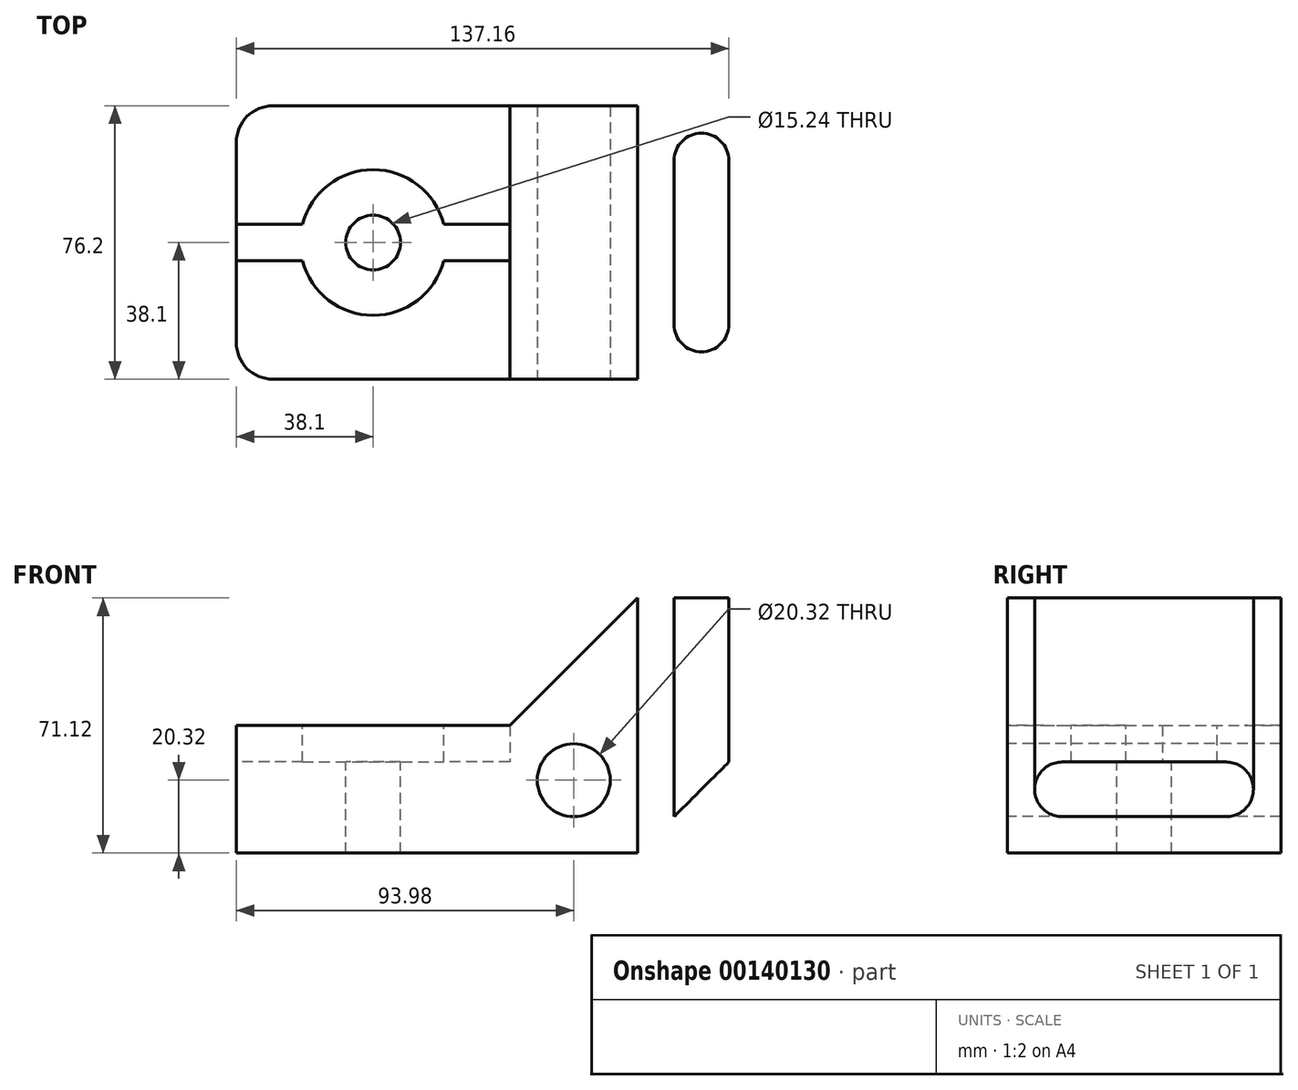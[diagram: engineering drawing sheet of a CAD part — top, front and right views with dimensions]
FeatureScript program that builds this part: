
annotation { "Feature Type Name" : "Feature", "Feature Type Description" : "" }
export const myFeature = defineFeature(function(context is Context, id is Id, definition is map)
    precondition{}
    {
        {
            var Q0;
            Q0=qCreatedBy(makeId("Top.planeOp"),FACE);
            var sketch = newSketch(context, id + "F0", { "sketchPlane" : qUnion([Q0])});
            skLineSegment(sketch, "E0.bottom", {"start": v(0, 0) * mm, "end": v(76.2, 0) * mm});
            skLineSegment(sketch, "E0.top", {"start": v(0, 76.2) * mm, "end": v(76.2, 76.2) * mm});
            skLineSegment(sketch, "E0.left", {"start": v(0, 0) * mm, "end": v(0, 76.2) * mm});
            skLineSegment(sketch, "E0.right", {"start": v(76.2, 0) * mm, "end": v(76.2, 76.2) * mm});
            skLineSegment(sketch, "E1.bottom", {"start": v(76.2, 76.2) * mm, "end": v(147.32, 76.2) * mm});
            skLineSegment(sketch, "E1.top", {"start": v(76.2, 0) * mm, "end": v(147.32, 0) * mm});
            skLineSegment(sketch, "E1.left", {"start": v(76.2, 76.2) * mm, "end": v(76.2, 0) * mm});
            skLineSegment(sketch, "E1.right", {"start": v(147.32, 76.2) * mm, "end": v(147.32, 0) * mm});
            skSolve(sketch);
        }
        {
            var Q0;
            Q0=makeQuery(id+"F0.imprint","IMPRINT",FACE,{"disambiguationData":[TD([[makeQuery(id+"F0.imprint","IMPRINT",EDGE,{"derivedFrom":sQuery(id+"F0.wireOp",EDGE,"E0.bottom")}),1.0]])]});
            extrude(context, id + "F1", {"entities" : qUnion([Q0]), "depth" : 35.56 * mm});
        }
        {
            var Q0;
            Q0=makeQuery(id+"F0.imprint","IMPRINT",FACE,{"disambiguationData":[TD([[makeQuery(id+"F0.imprint","IMPRINT",EDGE,{"derivedFrom":sQuery(id+"F0.wireOp",EDGE,"E1.bottom")}),-1.0]])]});
            extrude(context, id + "F2", {"entities" : qUnion([Q0]), "operationType" : NewBodyOperationType.ADD, "depth" : 71.12 * mm});
        }
        {
            var Q0;
            Q0=makeQuery(id+"F2.boolean.opBoolean","MERGE",FACE,{"derivedFrom":[makeQuery(id+"F1.opExtrude","SWEPT_FACE",FACE,{"disambiguationData":[OSD([sQuery(id+"F0.wireOp",EDGE,"E0.bottom")])]}),makeQuery(id+"F2.opExtrude","SWEPT_FACE",FACE,{"disambiguationData":[OSD([sQuery(id+"F0.wireOp",EDGE,"E1.top")])]})]});
            var sketch = newSketch(context, id + "F3", { "sketchPlane" : qUnion([Q0])});
            skLineSegment(sketch, "E2", {"start": v(147.32, 0) * mm, "end": v(111.76, 0) * mm});
            skLineSegment(sketch, "E3", {"start": v(111.76, 0) * mm, "end": v(147.32, 35.56) * mm});
            skLineSegment(sketch, "E4", {"start": v(147.32, 35.56) * mm, "end": v(147.32, 0) * mm});
            skLineSegment(sketch, "E5", {"start": v(76.2, 35.56) * mm, "end": v(111.76, 71.12) * mm});
            skLineSegment(sketch, "E6", {"start": v(111.76, 71.12) * mm, "end": v(76.2, 71.12) * mm});
            skLineSegment(sketch, "E7", {"start": v(76.2, 71.12) * mm, "end": v(76.2, 35.56) * mm});
            skSolve(sketch);
        }
        {
            var Q0;
            Q0=makeQuery(id+"F3.imprint","IMPRINT",FACE,{"disambiguationData":[TD([[makeQuery(id+"F3.imprint","IMPRINT",EDGE,{"derivedFrom":sQuery(id+"F3.wireOp",EDGE,"E5")}),1.0]])]});
            var Q1;
            Q1=makeQuery(id+"F3.imprint","IMPRINT",FACE,{"disambiguationData":[TD([[makeQuery(id+"F3.imprint","IMPRINT",EDGE,{"derivedFrom":sQuery(id+"F3.wireOp",EDGE,"E2")}),1.0]])]});
            extrude(context, id + "F4", {"entities" : qUnion([Q0, Q1]), "operationType" : NewBodyOperationType.REMOVE, "endBound" : BoundingType.THROUGH_ALL, "oppositeDirection" : true, "depth" : 25.4 * mm});
        }
        {
            var Q0;
            Q0=makeQuery(id+"F2.boolean.opBoolean","MERGE",FACE,{"derivedFrom":[makeQuery(id+"F1.opExtrude","SWEPT_FACE",FACE,{"disambiguationData":[OSD([sQuery(id+"F0.wireOp",EDGE,"E0.bottom")])]}),makeQuery(id+"F2.opExtrude","SWEPT_FACE",FACE,{"disambiguationData":[OSD([sQuery(id+"F0.wireOp",EDGE,"E1.top")])]})]});
            var sketch = newSketch(context, id + "F5", { "sketchPlane" : qUnion([Q0])});
            skCircle(sketch, "E8", {"center": v(93.98, 20.32) * mm, "radius": 10.16 * mm});
            skSolve(sketch);
        }
        {
            var Q0;
            Q0=makeQuery(id+"F5.imprint","IMPRINT",FACE,{"disambiguationData":[TD([[makeQuery(id+"F5.imprint","IMPRINT",EDGE,{"derivedFrom":sQuery(id+"F5.wireOp",EDGE,"E8")}),1.0]])]});
            extrude(context, id + "F6", {"entities" : qUnion([Q0]), "operationType" : NewBodyOperationType.REMOVE, "endBound" : BoundingType.THROUGH_ALL, "oppositeDirection" : true, "depth" : 25.4 * mm});
        }
        {
            var Q0;
            Q0=makeQuery(id+"F2.opExtrude","CAP_FACE",FACE,{"disambiguationData":[OSD([sQuery(id+"F0.wireOp",EDGE,"E1.bottom"),sQuery(id+"F0.wireOp",EDGE,"E1.top"),sQuery(id+"F0.wireOp",EDGE,"E1.left"),sQuery(id+"F0.wireOp",EDGE,"E1.right")])],"isStart":false});
            var sketch = newSketch(context, id + "F7", { "sketchPlane" : qUnion([Q0])});
            skLineSegment(sketch, "E9", {"start": v(147.32, 76.2) * mm, "end": v(129.54, 76.2) * mm, "construction": true});
            skLineSegment(sketch, "E10", {"start": v(129.54, 60.96) * mm, "end": v(129.54, 15.24) * mm, "construction": true});
            skLineSegment(sketch, "E11", {"start": v(129.54, 0) * mm, "end": v(147.32, 0) * mm, "construction": true});
            skPoint(sketch, "E12", {"position": v(129.54, 60.96) * mm});
            skPoint(sketch, "E13", {"position": v(129.54, 15.24) * mm});
            skArc(sketch, "E14.0.startCap", {"start": v(121.92, 60.96) * mm, "mid": v(129.54, 68.58) * mm, "end": v(137.16, 60.96) * mm});
            skArc(sketch, "E14.0.endCap", {"start": v(137.16, 15.24) * mm, "mid": v(129.54, 7.62) * mm, "end": v(121.92, 15.24) * mm});
            skLineSegment(sketch, "E14.0.left", {"start": v(137.16, 60.96) * mm, "end": v(137.16, 15.24) * mm});
            skLineSegment(sketch, "E14.0.right", {"start": v(121.92, 60.96) * mm, "end": v(121.92, 15.24) * mm});
            skSolve(sketch);
        }
        {
            var Q0;
            Q0=makeQuery(id+"F7.imprint","IMPRINT",FACE,{"disambiguationData":[TD([[makeQuery(id+"F7.imprint","IMPRINT",EDGE,{"derivedFrom":sQuery(id+"F7.wireOp",EDGE,"E14.0.startCap")}),-1.0]])]});
            extrude(context, id + "F8", {"entities" : qUnion([Q0]), "operationType" : NewBodyOperationType.REMOVE, "endBound" : BoundingType.THROUGH_ALL, "oppositeDirection" : true, "depth" : 25.4 * mm});
        }
        {
            var Q0;
            Q0=makeQuery(id+"F1.opExtrude","CAP_FACE",FACE,{"disambiguationData":[OSD([sQuery(id+"F0.wireOp",EDGE,"E0.bottom"),sQuery(id+"F0.wireOp",EDGE,"E0.top"),sQuery(id+"F0.wireOp",EDGE,"E0.left"),sQuery(id+"F0.wireOp",EDGE,"E1.left")])],"isStart":false});
            var sketch = newSketch(context, id + "F9", { "sketchPlane" : qUnion([Q0])});
            skLineSegment(sketch, "E15", {"start": v(0, 0) * mm, "end": v(38.1, 0) * mm, "construction": true});
            skLineSegment(sketch, "E16", {"start": v(38.1, 0) * mm, "end": v(38.1, 38.1) * mm, "construction": true});
            skPoint(sketch, "E17", {"position": v(38.1, 38.1) * mm});
            skSolve(sketch);
        }
        {
            var Q0;
            Q0=sQuery(id+"F9.wireOp",VERTEX,"E17");
            var Q1;
            Q1=makeQuery(id+"F1.opExtrude","SWEPT_BODY",BODY,{"disambiguationData":[OSD([sQuery(id+"F0.wireOp",EDGE,"E0.bottom"),sQuery(id+"F0.wireOp",EDGE,"E0.top"),sQuery(id+"F0.wireOp",EDGE,"E0.left"),sQuery(id+"F0.wireOp",EDGE,"E1.left")])]});
            hole(context, id + "F10", {"style" : HoleStyle.C_BORE, "endStyle" : HoleEndStyle.THROUGH, "holeDiameter" : 15.24 * mm, "cBoreDiameter" : 40.64 * mm, "cBoreDepth" : 10.16 * mm, "locations" : qUnion([Q0]), "scope" : qUnion([Q1]), "isTappedThrough" : true});
        }
        {
            var Q0;
            Q0=makeQuery(id+"F1.opExtrude","SWEPT_FACE",FACE,{"disambiguationData":[OSD([sQuery(id+"F0.wireOp",EDGE,"E0.left")])]});
            var sketch = newSketch(context, id + "F11", { "sketchPlane" : qUnion([Q0])});
            skLineSegment(sketch, "E18", {"start": v(-76.2, 0) * mm, "end": v(-38.1, 0) * mm, "construction": true});
            skLineSegment(sketch, "E19", {"start": v(-38.1, 0) * mm, "end": v(-38.1, 35.56) * mm, "construction": true});
            skLineSegment(sketch, "E20.bottom", {"start": v(-43.18, 35.56) * mm, "end": v(-33.02, 35.56) * mm});
            skLineSegment(sketch, "E20.top", {"start": v(-43.18, 25.4) * mm, "end": v(-33.02, 25.4) * mm});
            skLineSegment(sketch, "E20.left", {"start": v(-43.18, 35.56) * mm, "end": v(-43.18, 25.4) * mm});
            skLineSegment(sketch, "E20.right", {"start": v(-33.02, 35.56) * mm, "end": v(-33.02, 25.4) * mm});
            skSolve(sketch);
        }
        {
            var Q0;
            Q0 = qSketchRegion(id + "F11", true);
            var Q1;
            Q1=makeQuery(id+"F11.imprint","IMPRINT",FACE,{"disambiguationData":[TD([[makeQuery(id+"F11.imprint","IMPRINT",EDGE,{"derivedFrom":sQuery(id+"F11.wireOp",EDGE,"E20.bottom")}),1.0]])]});
            extrude(context, id + "F12", {"entities" : qUnion([Q0, Q1]), "operationType" : NewBodyOperationType.REMOVE, "oppositeDirection" : true, "depth" : 76.2 * mm});
        }
        {
            var Q0;
            Q0=makeQuery(id+"F1.opExtrude","SWEPT_EDGE",EDGE,{"disambiguationData":[OSD([sQuery(id+"F0.wireOp",EDGE,"E0.top"),sQuery(id+"F0.wireOp",EDGE,"E0.left")])]});
            var Q1;
            Q1=makeQuery(id+"F1.opExtrude","SWEPT_EDGE",EDGE,{"disambiguationData":[OSD([sQuery(id+"F0.wireOp",EDGE,"E0.bottom"),sQuery(id+"F0.wireOp",EDGE,"E0.left")])]});
            fillet(context, id + "F13", {"entities" : qUnion([Q0, Q1]), "radius" : 10.16 * mm, "tangentPropagation" : true, "allowEdgeOverflow" : false});
        }
    });
